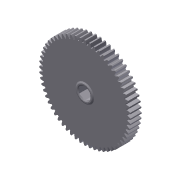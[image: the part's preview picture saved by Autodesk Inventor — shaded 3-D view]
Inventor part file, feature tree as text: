
AUTODESK INVENTOR PART (.ipt)
format: ipt  version: 2011 (Build 150239000, 239)  size: 413,184 bytes
history: native  units: mm (DEFAULTED — no unit token found)
features: sketch x5, other x4, extrude x3, plane x3, revolve x1, projected_geometry x1
ambient origin geometry x8: Origin, YZ Plane, XZ Plane, XY Plane, X Axis, Y Axis, Z Axis, Center Point
bodies: Solid1 (feature_tree)
feature tree (17):
  other  "Gear 60T 20dp 375hex"
  extrude  "Extrusion1"  Depth=9.525mm TaperAngle=0.0deg
  plane  "Work Plane1"
  plane  "Work Plane2"
  plane  "Work Plane3"
  other  "Spur Gear"
  extrude  "Extrusion2"  Depth=76.2mm TaperAngle=0.0deg
  extrude  "Extrusion3"  TaperAngle=0.0deg  [1 undecoded]
  revolve  "Revolution1"  [1 undecoded]
  sketch  "Sketch1"  dims[d0=78.74mm d1=9.525mm d2=0.0mm]
  sketch  "Sketch2"  dims[d3=76.2mm d4=76.2mm d5=0.0mm]
  other  "Srf1"
  sketch  "Sketch3"  dims[d6=0.0mm d7=0.523599mm d9=0.0mm]
  sketch  "Sketch4"  dims[d14=0.0mm d15=190.5mm d16=0.0mm]
  sketch  "Sketch5"  dims[d17=0.0mm d18=0.0mm d19=190.5mm d20=15.9004mm d21=0.635mm d22=0.0mm d23=9.525mm d24=0.635mm d25=0.0mm d26=5.070181mm d27=6.35mm d28=0.889mm d29=5.070181mm d30=2.54mm d31=90.0deg]
  projected_geometry  "Projected Loop1"
  other  "Pitch Diameter"
note: 2 required parameter values undecoded (feature->parameter linkage not recoverable at this tier; creation-order binding heuristic only, values carry confidence <= 0.55)